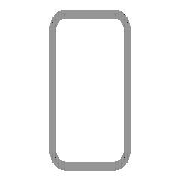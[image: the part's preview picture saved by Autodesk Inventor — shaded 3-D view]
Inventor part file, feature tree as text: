
AUTODESK INVENTOR PART (.ipt)
format: ipt  version: 2025 (Build 290162010, 162A)  size: 133,120 bytes
history: native  units: mm (DEFAULTED — no unit token found)
features: other x4, sketch x1, plane x1
ambient origin geometry x8: Origin, YZ Plane, XZ Plane, XY Plane, X Axis, Y Axis, Z Axis, Center Point
bodies: Solid1 (feature_tree), Body (feature_tree)
feature tree (6):
  parser-record x1  (decoder bookkeeping rows leaked as tree rows — omitted from the tree; the rows remain in map.json)
  other  "Driven Length"
  other  "Start Plane"
  other  "End Plane"
  sketch  "Sketch3"  dims[d3=600.0mm d4=0.0mm d7=6.0mm d9=40.0mm d11=80.0mm d12=3.0mm d13=-0.0mm d14=600.0mm d15=20.0mm d16=40.0mm d17=90.0deg d18=600.0mm]
  plane  "Work Plane3"
